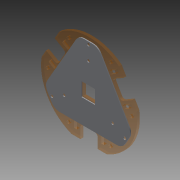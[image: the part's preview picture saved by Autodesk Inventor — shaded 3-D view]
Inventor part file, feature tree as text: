
AUTODESK INVENTOR PART (.ipt)
format: ipt  version: 2015 (Build 190159000, 159)  size: 385,024 bytes
history: native  units: mm
features: other x4, extrude x1, sketch x1, projected_geometry x1
ambient origin geometry x8: Origin, YZ Plane, XZ Plane, XY Plane, X Axis, Y Axis, Z Axis, Center Point
bodies: Solid1 (feature_tree)
feature tree (7):
  other  "top plate.ipt"
  extrude  "Extrusion1"  Depth=1.0mm
  other  "TaggingFeature1"
  sketch  "Sketch1"  dims[d0=10.0mm d1=1.0mm d2=1.0mm d3=3.2mm d7=3.0mm d8=3.2mm d9=120.0deg d10=120.0deg d11=3.0mm d12=3.0mm d13=3.2mm d14=3.2mm d15=3.2mm d16=3.2mm d17=10.0mm d18=10.0mm d19=1.0mm d20=0.0mm]
  other  "Solid1::top plate.ipt"
  other  "Srf1"
  projected_geometry  "Project Cut Edges1"
